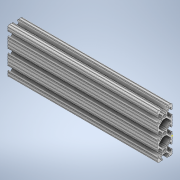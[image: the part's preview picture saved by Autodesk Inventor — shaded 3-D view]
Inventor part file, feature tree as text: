
AUTODESK INVENTOR PART (.ipt)
format: ipt  version: 2020 (Build 240168000, 168)  size: 381,440 bytes
history: native  units: in
note: dims shown in document units (in); Inventor stores cm internally (conversion verified against a paired STEP export)
features: sketch x2, extrude x1
ambient origin geometry x8: Origin, YZ Plane, XZ Plane, XY Plane, X Axis, Y Axis, Z Axis, Center Point
bodies: Solid1 (feature_tree)
feature tree (3):
  extrude  "Extrusion1"  [1 undecoded]
  sketch  "Sketch2"
  sketch  "Sketch1"  dims[d0=10.0in d1=0.0in]
note: 1 required parameter value undecoded (feature->parameter linkage not recoverable at this tier; creation-order binding heuristic only, values carry confidence <= 0.55)
